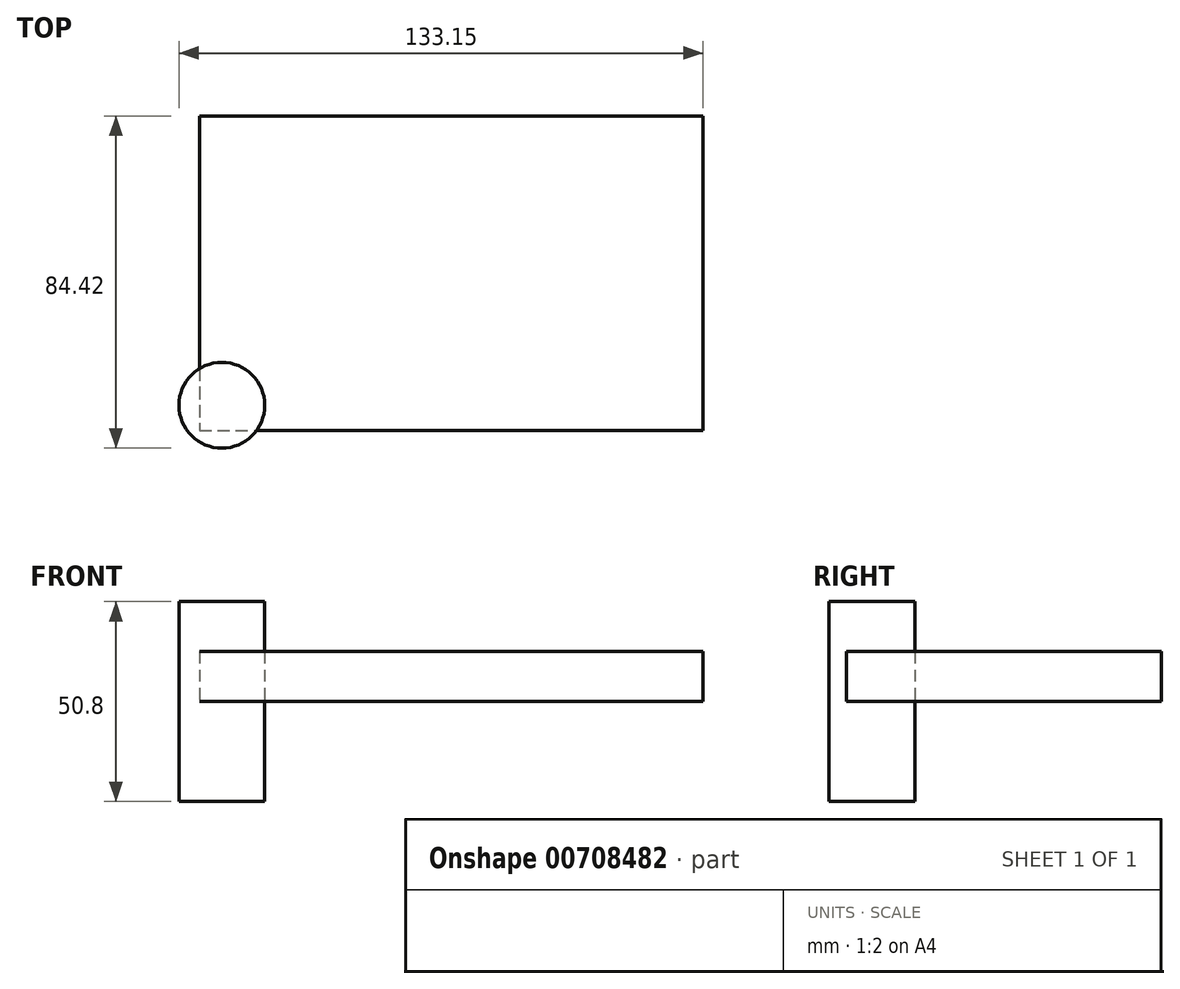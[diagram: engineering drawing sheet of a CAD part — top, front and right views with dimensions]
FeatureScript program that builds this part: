
annotation { "Feature Type Name" : "Feature", "Feature Type Description" : "" }
export const myFeature = defineFeature(function(context is Context, id is Id, definition is map)
    precondition{}
    {
        {
            var Q0;
            Q0=qCreatedBy(makeId("Top.planeOp"),FACE);
            var sketch = newSketch(context, id + "F0", { "sketchPlane" : qUnion([Q0])});
            skLineSegment(sketch, "E0.bottom", {"start": v(-5.66, 73.52) * mm, "end": v(122.25, 73.52) * mm});
            skLineSegment(sketch, "E0.top", {"start": v(-5.66, -6.45) * mm, "end": v(122.25, -6.45) * mm});
            skLineSegment(sketch, "E0.left", {"start": v(-5.66, 73.52) * mm, "end": v(-5.66, -6.45) * mm});
            skLineSegment(sketch, "E0.right", {"start": v(122.25, 73.52) * mm, "end": v(122.25, -6.45) * mm});
            skSolve(sketch);
        }
        {
            var Q0;
            Q0=makeQuery(id+"F0.imprint","IMPRINT",FACE,{"disambiguationData":[TD([[makeQuery(id+"F0.imprint","IMPRINT",EDGE,{"derivedFrom":sQuery(id+"F0.wireOp",EDGE,"E0.bottom")}),-1.0]])]});
            extrude(context, id + "F1", {"entities" : qUnion([Q0]), "depth" : 12.7 * mm, "offsetDistance" : 25.4 * mm});
        }
        {
            var Q0;
            Q0=qCreatedBy(makeId("Top.planeOp"),FACE);
            var sketch = newSketch(context, id + "F2", { "sketchPlane" : qUnion([Q0])});
            skCircle(sketch, "E1", {"center": v(0, 0) * mm, "radius": 10.9 * mm});
            skSolve(sketch);
        }
        {
            var Q0;
            Q0=makeQuery(id+"F2.imprint","IMPRINT",FACE,{"disambiguationData":[TD([[makeQuery(id+"F2.imprint","IMPRINT",EDGE,{"derivedFrom":sQuery(id+"F2.wireOp",EDGE,"E1")}),1.0]])]});
            extrude(context, id + "F3", {"entities" : qUnion([Q0]), "depth" : 25.4 * mm, "offsetDistance" : 25.4 * mm, "hasSecondDirection" : true, "secondDirectionOppositeDirection" : true, "secondDirectionDepth" : 25.4 * mm});
        }
    });
